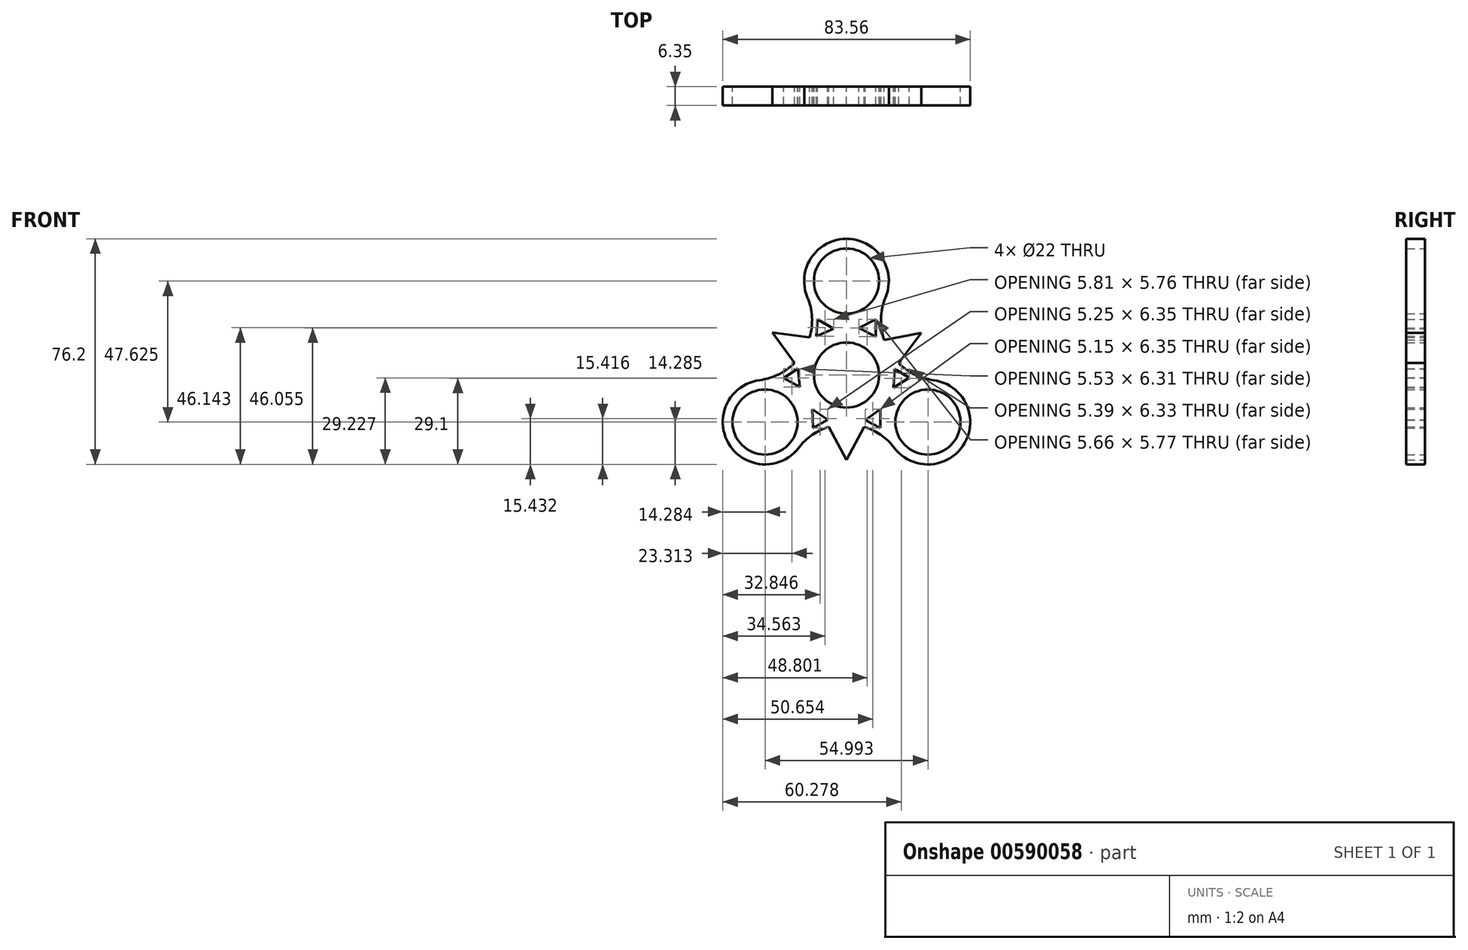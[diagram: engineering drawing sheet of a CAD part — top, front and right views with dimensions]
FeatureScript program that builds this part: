
annotation { "Feature Type Name" : "Feature", "Feature Type Description" : "" }
export const myFeature = defineFeature(function(context is Context, id is Id, definition is map)
    precondition{}
    {
        {
            var Q0;
            Q0=qCreatedBy(makeId("Front.planeOp"),FACE);
            var sketch = newSketch(context, id + "F0", { "sketchPlane" : qUnion([Q0])});
            skCircle(sketch, "E0.0", {"center": v(0, 31.75) * mm, "radius": 14.29 * mm});
            skCircle(sketch, "E1.0", {"center": v(0, 31.75) * mm, "radius": 11 * mm});
            skCircle(sketch, "E2.0", {"center": v(0, 0) * mm, "radius": 14.29 * mm});
            skCircle(sketch, "E3.0", {"center": v(0, 0) * mm, "radius": 11 * mm});
            skCircle(sketch, "E4.0", {"center": v(-27.5, -15.87) * mm, "radius": 14.29 * mm});
            skCircle(sketch, "E5.0", {"center": v(-27.5, -15.87) * mm, "radius": 11 * mm});
            skCircle(sketch, "E6.0", {"center": v(27.5, -15.88) * mm, "radius": 14.29 * mm});
            skCircle(sketch, "E7.0", {"center": v(27.5, -15.88) * mm, "radius": 11 * mm});
            skLineSegment(sketch, "E8.0", {"start": v(25.2, 14.23) * mm, "end": v(17.58, 4.08) * mm});
            skLineSegment(sketch, "E9.0", {"start": v(12.74, 11.8) * mm, "end": v(25.2, 14.23) * mm});
            skLineSegment(sketch, "E10.0", {"start": v(-12.44, 12.75) * mm, "end": v(-25.04, 14.35) * mm});
            skPoint(sketch, "E11.0", {"position": v(-21.31, 9.21) * mm});
            skLineSegment(sketch, "E12.0", {"start": v(-25.04, 14.35) * mm, "end": v(-17.58, 4.08) * mm});
            skLineSegment(sketch, "E13.0", {"start": v(-4.3, 15.65) * mm, "end": v(-9.79, 18.87) * mm});
            skLineSegment(sketch, "E14.0", {"start": v(-9.79, 18.87) * mm, "end": v(-10.12, 13.1) * mm});
            skLineSegment(sketch, "E15.0", {"start": v(-10.12, 13.1) * mm, "end": v(-4.3, 15.65) * mm});
            skLineSegment(sketch, "E16.0", {"start": v(9.85, 13.01) * mm, "end": v(4.2, 15.9) * mm});
            skLineSegment(sketch, "E17.0", {"start": v(4.2, 15.9) * mm, "end": v(9.85, 18.78) * mm});
            skLineSegment(sketch, "E18.0", {"start": v(9.85, 18.78) * mm, "end": v(9.85, 13.01) * mm});
            skLineSegment(sketch, "E19.0", {"start": v(16.26, 2.1) * mm, "end": v(21.2, -0.88) * mm});
            skLineSegment(sketch, "E20.0", {"start": v(15.8, -4.23) * mm, "end": v(16.26, 2.1) * mm});
            skLineSegment(sketch, "E21.0", {"start": v(21.2, -0.88) * mm, "end": v(15.8, -4.23) * mm});
            skArc(sketch, "E22.0", {"start": v(-29.33, -1.7) * mm, "mid": v(-14.35, 8.29) * mm, "end": v(-13.19, 26.26) * mm});
            skArc(sketch, "E23.0", {"start": v(13.19, 26.26) * mm, "mid": v(14.35, 8.29) * mm, "end": v(29.33, -1.7) * mm});
            skLineSegment(sketch, "E24.0", {"start": v(0, -28.69) * mm, "end": v(5.93, -17.45) * mm});
            skLineSegment(sketch, "E25.0", {"start": v(-5.93, -17.45) * mm, "end": v(0, -28.69) * mm});
            skArc(sketch, "E26.0", {"start": v(16.14, -24.55) * mm, "mid": v(0, -16.57) * mm, "end": v(-16.14, -24.55) * mm});
            skLineSegment(sketch, "E27.0", {"start": v(-16.42, 2.22) * mm, "end": v(-15.7, -4.09) * mm});
            skLineSegment(sketch, "E28.0", {"start": v(-21.23, -0.96) * mm, "end": v(-16.42, 2.22) * mm});
            skLineSegment(sketch, "E29.0", {"start": v(-15.7, -4.09) * mm, "end": v(-21.23, -0.96) * mm});
            skLineSegment(sketch, "E30.0", {"start": v(-6.3, -15.14) * mm, "end": v(-11.56, -11.57) * mm});
            skLineSegment(sketch, "E31.0", {"start": v(-11.36, -17.92) * mm, "end": v(-6.3, -15.14) * mm});
            skLineSegment(sketch, "E32.0", {"start": v(-11.56, -11.57) * mm, "end": v(-11.36, -17.92) * mm});
            skLineSegment(sketch, "E33.0", {"start": v(11.45, -11.55) * mm, "end": v(6.3, -15.26) * mm});
            skLineSegment(sketch, "E34.0", {"start": v(11.42, -17.9) * mm, "end": v(11.45, -11.55) * mm});
            skLineSegment(sketch, "E35.0", {"start": v(6.3, -15.26) * mm, "end": v(11.42, -17.9) * mm});
            skSolve(sketch);
        }
        {
            var Q0;
            Q0 = qSketchRegion(id + "F0", true);
            var Q1;
            Q1=makeQuery(id+"F0.imprint","IMPRINT",FACE,{"disambiguationData":[TD([[makeQuery(id+"F0.imprint","IMPRINT",EDGE,{"derivedFrom":sQuery(id+"F0.wireOp",EDGE,"E2.0")}),1.0]])]});
            extrude(context, id + "F1", {"entities" : qUnion([Q0, Q1]), "depth" : 6.35 * mm, "offsetDistance" : 25.4 * mm});
        }
        {
            var Q0;
            Q0=makeQuery(id+"FPAsyPKfHc9TFCi_3.boolean.opBoolean","MERGE",FACE,{"derivedFrom":[makeQuery(id+"F1.opExtrude","CAP_FACE",FACE,{"disambiguationData":[OSD([sQuery(id+"F0.wireOp",EDGE,"E0.0"),sQuery(id+"F0.wireOp",EDGE,"E1.0"),sQuery(id+"F0.wireOp",EDGE,"E2.0"),sQuery(id+"F0.wireOp",EDGE,"E4.0"),sQuery(id+"F0.wireOp",EDGE,"E5.0"),sQuery(id+"F0.wireOp",EDGE,"E6.0"),sQuery(id+"F0.wireOp",EDGE,"E7.0"),sQuery(id+"F0.wireOp",EDGE,"E8.0"),sQuery(id+"F0.wireOp",EDGE,"E9.0"),sQuery(id+"F0.wireOp",EDGE,"E10.0"),sQuery(id+"F0.wireOp",EDGE,"E12.0"),sQuery(id+"F0.wireOp",EDGE,"E13.0"),sQuery(id+"F0.wireOp",EDGE,"E14.0"),sQuery(id+"F0.wireOp",EDGE,"E15.0"),sQuery(id+"F0.wireOp",EDGE,"E16.0"),sQuery(id+"F0.wireOp",EDGE,"E17.0"),sQuery(id+"F0.wireOp",EDGE,"E18.0"),sQuery(id+"F0.wireOp",EDGE,"E19.0"),sQuery(id+"F0.wireOp",EDGE,"E20.0"),sQuery(id+"F0.wireOp",EDGE,"E21.0"),sQuery(id+"F0.wireOp",EDGE,"E22.0"),sQuery(id+"F0.wireOp",EDGE,"E23.0"),sQuery(id+"F0.wireOp",EDGE,"E24.0"),sQuery(id+"F0.wireOp",EDGE,"E25.0"),sQuery(id+"F0.wireOp",EDGE,"E26.0"),sQuery(id+"F0.wireOp",EDGE,"E27.0"),sQuery(id+"F0.wireOp",EDGE,"E28.0"),sQuery(id+"F0.wireOp",EDGE,"E29.0"),sQuery(id+"F0.wireOp",EDGE,"E30.0"),sQuery(id+"F0.wireOp",EDGE,"E31.0"),sQuery(id+"F0.wireOp",EDGE,"E32.0"),sQuery(id+"F0.wireOp",EDGE,"E33.0"),sQuery(id+"F0.wireOp",EDGE,"E34.0"),sQuery(id+"F0.wireOp",EDGE,"E35.0")])],"isStart":false}),makeQuery(id+"FPAsyPKfHc9TFCi_3.opExtrude","CAP_FACE",FACE,{"disambiguationData":[OSD([sQuery(id+"FSH52HT0z7hYMNx_3.wireOp",EDGE,"f33444f0-0c35-4c04-ba17-0b5da8cf25b7.0"),sQuery(id+"FSH52HT0z7hYMNx_3.wireOp",EDGE,"d82499fd-bfa2-4744-9be0-edfae4d8cac3.0.0")])],"isStart":false})]});
            extrude(context, id + "F2", {"entities" : qUnion([Q0]), "operationType" : NewBodyOperationType.ADD, "depth" : 6.35 * mm, "offsetDistance" : 25.4 * mm});
        }
        {
            var Q0;
            Q0=makeQuery(id+"FPAsyPKfHc9TFCi_3.boolean.opBoolean","MERGE",FACE,{"derivedFrom":[makeQuery(id+"F1.opExtrude","CAP_FACE",FACE,{"disambiguationData":[OSD([sQuery(id+"F0.wireOp",EDGE,"E0.0"),sQuery(id+"F0.wireOp",EDGE,"E1.0"),sQuery(id+"F0.wireOp",EDGE,"E2.0"),sQuery(id+"F0.wireOp",EDGE,"E4.0"),sQuery(id+"F0.wireOp",EDGE,"E5.0"),sQuery(id+"F0.wireOp",EDGE,"E6.0"),sQuery(id+"F0.wireOp",EDGE,"E7.0"),sQuery(id+"F0.wireOp",EDGE,"E8.0"),sQuery(id+"F0.wireOp",EDGE,"E9.0"),sQuery(id+"F0.wireOp",EDGE,"E10.0"),sQuery(id+"F0.wireOp",EDGE,"E12.0"),sQuery(id+"F0.wireOp",EDGE,"E13.0"),sQuery(id+"F0.wireOp",EDGE,"E14.0"),sQuery(id+"F0.wireOp",EDGE,"E15.0"),sQuery(id+"F0.wireOp",EDGE,"E16.0"),sQuery(id+"F0.wireOp",EDGE,"E17.0"),sQuery(id+"F0.wireOp",EDGE,"E18.0"),sQuery(id+"F0.wireOp",EDGE,"E19.0"),sQuery(id+"F0.wireOp",EDGE,"E20.0"),sQuery(id+"F0.wireOp",EDGE,"E21.0"),sQuery(id+"F0.wireOp",EDGE,"E22.0"),sQuery(id+"F0.wireOp",EDGE,"E23.0"),sQuery(id+"F0.wireOp",EDGE,"E24.0"),sQuery(id+"F0.wireOp",EDGE,"E25.0"),sQuery(id+"F0.wireOp",EDGE,"E26.0"),sQuery(id+"F0.wireOp",EDGE,"E27.0"),sQuery(id+"F0.wireOp",EDGE,"E28.0"),sQuery(id+"F0.wireOp",EDGE,"E29.0"),sQuery(id+"F0.wireOp",EDGE,"E30.0"),sQuery(id+"F0.wireOp",EDGE,"E31.0"),sQuery(id+"F0.wireOp",EDGE,"E32.0"),sQuery(id+"F0.wireOp",EDGE,"E33.0"),sQuery(id+"F0.wireOp",EDGE,"E34.0"),sQuery(id+"F0.wireOp",EDGE,"E35.0")])],"isStart":true}),makeQuery(id+"FPAsyPKfHc9TFCi_3.opExtrude","CAP_FACE",FACE,{"disambiguationData":[OSD([sQuery(id+"FSH52HT0z7hYMNx_3.wireOp",EDGE,"f33444f0-0c35-4c04-ba17-0b5da8cf25b7.0"),sQuery(id+"FSH52HT0z7hYMNx_3.wireOp",EDGE,"d82499fd-bfa2-4744-9be0-edfae4d8cac3.0.0")])],"isStart":true})]});
            extrude(context, id + "F3", {"entities" : qUnion([Q0]), "operationType" : NewBodyOperationType.REMOVE, "oppositeDirection" : true, "depth" : 6.35 * mm, "offsetDistance" : 25.4 * mm});
        }
        {
            var Q0;
            Q0=makeQuery(id+"F3.boolean.opBoolean","COPY",FACE,{"derivedFrom":makeQuery(id+"F3.opExtrude","CAP_FACE",FACE,{"disambiguationData":[OSD([sQuery(id+"F0.wireOp",EDGE,"E0.0"),sQuery(id+"F0.wireOp",EDGE,"E1.0"),sQuery(id+"F0.wireOp",EDGE,"E2.0"),sQuery(id+"F0.wireOp",EDGE,"E4.0"),sQuery(id+"F0.wireOp",EDGE,"E5.0"),sQuery(id+"F0.wireOp",EDGE,"E6.0"),sQuery(id+"F0.wireOp",EDGE,"E7.0"),sQuery(id+"F0.wireOp",EDGE,"E8.0"),sQuery(id+"F0.wireOp",EDGE,"E9.0"),sQuery(id+"F0.wireOp",EDGE,"E10.0"),sQuery(id+"F0.wireOp",EDGE,"E12.0"),sQuery(id+"F0.wireOp",EDGE,"E13.0"),sQuery(id+"F0.wireOp",EDGE,"E14.0"),sQuery(id+"F0.wireOp",EDGE,"E15.0"),sQuery(id+"F0.wireOp",EDGE,"E16.0"),sQuery(id+"F0.wireOp",EDGE,"E17.0"),sQuery(id+"F0.wireOp",EDGE,"E18.0"),sQuery(id+"F0.wireOp",EDGE,"E19.0"),sQuery(id+"F0.wireOp",EDGE,"E20.0"),sQuery(id+"F0.wireOp",EDGE,"E21.0"),sQuery(id+"F0.wireOp",EDGE,"E22.0"),sQuery(id+"F0.wireOp",EDGE,"E23.0"),sQuery(id+"F0.wireOp",EDGE,"E24.0"),sQuery(id+"F0.wireOp",EDGE,"E25.0"),sQuery(id+"F0.wireOp",EDGE,"E26.0"),sQuery(id+"F0.wireOp",EDGE,"E27.0"),sQuery(id+"F0.wireOp",EDGE,"E28.0"),sQuery(id+"F0.wireOp",EDGE,"E29.0"),sQuery(id+"F0.wireOp",EDGE,"E30.0"),sQuery(id+"F0.wireOp",EDGE,"E31.0"),sQuery(id+"F0.wireOp",EDGE,"E32.0"),sQuery(id+"F0.wireOp",EDGE,"E33.0"),sQuery(id+"F0.wireOp",EDGE,"E34.0"),sQuery(id+"F0.wireOp",EDGE,"E35.0")])],"isStart":false})});
            var sketch = newSketch(context, id + "F4", { "sketchPlane" : qUnion([Q0])});
            skCircle(sketch, "E36", {"center": v(0, 0) * mm, "radius": 11 * mm});
            skSolve(sketch);
        }
        {
            var Q0;
            Q0=makeQuery(id+"F4.imprint","IMPRINT",FACE,{"disambiguationData":[TD([[makeQuery(id+"F4.imprint","IMPRINT",EDGE,{"derivedFrom":sQuery(id+"F4.wireOp",EDGE,"E36")}),-1.0]])]});
            extrude(context, id + "F5", {"entities" : qUnion([Q0]), "operationType" : NewBodyOperationType.REMOVE, "oppositeDirection" : true, "depth" : 6.35 * mm, "offsetDistance" : 25.4 * mm});
        }
    });
